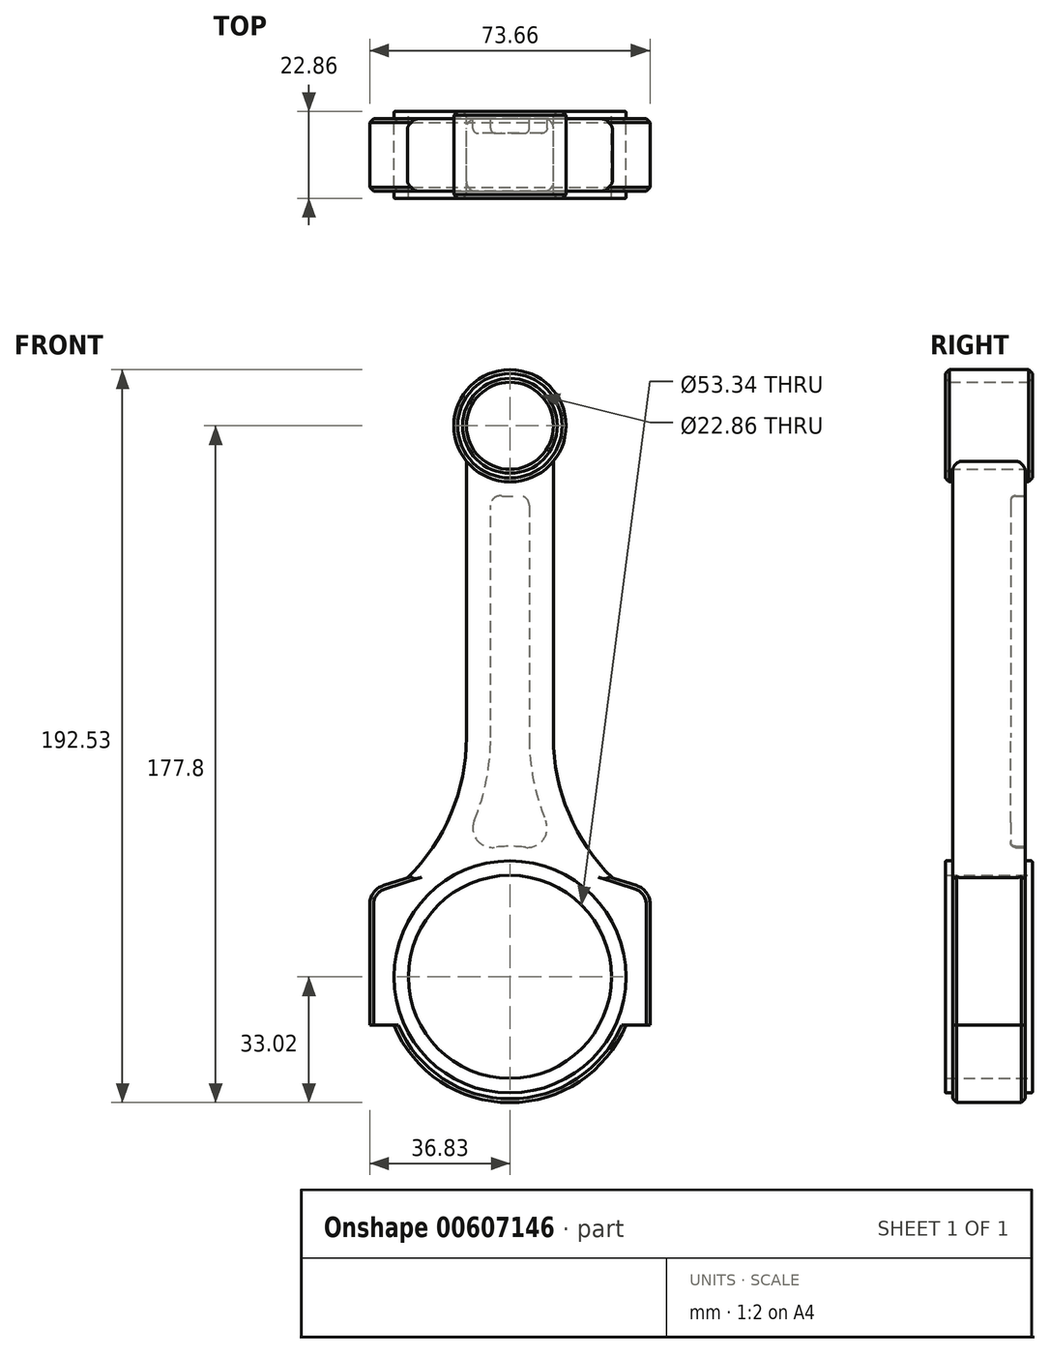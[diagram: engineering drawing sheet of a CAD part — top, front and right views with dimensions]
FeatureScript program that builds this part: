
annotation { "Feature Type Name" : "Feature", "Feature Type Description" : "" }
export const myFeature = defineFeature(function(context is Context, id is Id, definition is map)
    precondition{}
    {
        {
            var Q0;
            Q0=qCreatedBy(makeId("Front.planeOp"),FACE);
            var sketch = newSketch(context, id + "F0", { "sketchPlane" : qUnion([Q0])});
            skCircle(sketch, "E0", {"center": v(0, 0) * mm, "radius": 26.67 * mm});
            skCircle(sketch, "E1.0", {"center": v(0, 0) * mm, "radius": 30.48 * mm});
            skCircle(sketch, "E2.0", {"center": v(0, 0) * mm, "radius": 33.02 * mm});
            skLineSegment(sketch, "E3", {"start": v(-26.67, 0) * mm, "end": v(-36.83, 0) * mm});
            skLineSegment(sketch, "E4", {"start": v(-36.83, 0) * mm, "end": v(-36.83, 22.86) * mm});
            skLineSegment(sketch, "E5", {"start": v(0, 0) * mm, "end": v(0, 144.78) * mm, "construction": true});
            skCircle(sketch, "E6", {"center": v(0, 144.78) * mm, "radius": 11.43 * mm});
            skCircle(sketch, "E7.0", {"center": v(0, 144.78) * mm, "radius": 14.73 * mm});
            skLineSegment(sketch, "E8", {"start": v(-11.43, 144.78) * mm, "end": v(-11.43, 62.91) * mm});
            skLineSegment(sketch, "E9.MirrorCS", {"start": v(11.43, 144.78) * mm, "end": v(11.43, 62.91) * mm});
            skLineSegment(sketch, "E10.MirrorCS", {"start": v(36.83, 0) * mm, "end": v(36.83, 22.86) * mm});
            skLineSegment(sketch, "E11.MirrorCS", {"start": v(26.67, 0) * mm, "end": v(36.83, 0) * mm});
            skLineSegment(sketch, "E12", {"start": v(-36.83, 22.86) * mm, "end": v(-26.89, 26.05) * mm});
            skLineSegment(sketch, "E13.MirrorCS", {"start": v(36.83, 22.86) * mm, "end": v(26.89, 26.05) * mm});
            skArc(sketch, "E14", {"start": v(-26.89, 26.05) * mm, "mid": v(-15.45, 42.93) * mm, "end": v(-11.43, 62.91) * mm});
            skArc(sketch, "E15.MirrorCS", {"start": v(26.89, 26.05) * mm, "mid": v(15.45, 42.93) * mm, "end": v(11.43, 62.91) * mm});
            skLineSegment(sketch, "E16", {"start": v(-36.83, 0) * mm, "end": v(-36.83, -12.7) * mm});
            skLineSegment(sketch, "E17", {"start": v(-36.83, -12.7) * mm, "end": v(-30.48, -12.7) * mm});
            skLineSegment(sketch, "E18.MirrorCS", {"start": v(36.83, 0) * mm, "end": v(36.83, -12.7) * mm});
            skLineSegment(sketch, "E19.MirrorCS", {"start": v(36.83, -12.7) * mm, "end": v(30.48, -12.7) * mm});
            skSolve(sketch);
        }
        {
            var Q0;
            {var subQ13=sQuery(id+"F0.wireOp",EDGE,"E4");Q0=makeQuery(id+"F0.imprint","IMPRINT",FACE,{"disambiguationData":[TD([[makeQuery(id+"F0.imprint","IMPRINT",EDGE,{"derivedFrom":subQ13}),-1.0]])]});}
            var Q1;
            {var subQ0=sQuery(id+"F0.wireOp",EDGE,"E3");var subQ1=sQuery(id+"F0.wireOp",EDGE,"E1.0");var subQ2=makeQuery(id+"F0.imprint","INTERSECT",VERTEX,{"derivedFrom":[subQ1,subQ0]});Q1=makeQuery(id+"F0.imprint","IMPRINT",FACE,{"disambiguationData":[TD([[makeQuery(id+"F0.imprint","IMPRINT",EDGE,{"disambiguationData":[TD([[subQ2,1.0]])],"derivedFrom":subQ1}),-1.0]])]});}
            extrude(context, id + "F1", {"entities" : qUnion([Q0, Q1]), "depth" : 19.05 * mm, "offsetDistance" : 25.4 * mm, "symmetric" : true});
        }
        {
            var Q0;
            {var subQ4=sQuery(id+"F0.wireOp",EDGE,"E16");Q0=makeQuery(id+"F0.imprint","IMPRINT",FACE,{"disambiguationData":[TD([[makeQuery(id+"F0.imprint","IMPRINT",EDGE,{"derivedFrom":subQ4}),1.0]])]});}
            var Q1;
            {var subQ5=sQuery(id+"F0.wireOp",EDGE,"E3");var subQ7=sQuery(id+"F0.wireOp",EDGE,"E1.0");var subQ8=makeQuery(id+"F0.imprint","INTERSECT",VERTEX,{"derivedFrom":[subQ7,subQ5]});Q1=makeQuery(id+"F0.imprint","IMPRINT",FACE,{"disambiguationData":[TD([[makeQuery(id+"F0.imprint","IMPRINT",EDGE,{"disambiguationData":[TD([[subQ8,-1.0]])],"derivedFrom":subQ7}),-1.0]])]});}
            var Q2;
            {var subQ4=sQuery(id+"F0.wireOp",EDGE,"E18.MirrorCS");Q2=makeQuery(id+"F0.imprint","IMPRINT",FACE,{"disambiguationData":[TD([[makeQuery(id+"F0.imprint","IMPRINT",EDGE,{"derivedFrom":subQ4}),-1.0]])]});}
            extrude(context, id + "F2", {"entities" : qUnion([Q0, Q1, Q2]), "depth" : 19.05 * mm, "offsetDistance" : 25.4 * mm, "symmetric" : true});
        }
        {
            var Q0;
            {var subQ0=sQuery(id+"F0.wireOp",EDGE,"E3");var subQ1=sQuery(id+"F0.wireOp",EDGE,"E0");var subQ2=makeQuery(id+"F0.imprint","INTERSECT",VERTEX,{"derivedFrom":[subQ1,subQ0]});Q0=makeQuery(id+"F0.imprint","IMPRINT",FACE,{"disambiguationData":[TD([[makeQuery(id+"F0.imprint","IMPRINT",EDGE,{"disambiguationData":[TD([[subQ2,1.0]])],"derivedFrom":subQ1}),-1.0]])]});}
            extrude(context, id + "F3", {"entities" : qUnion([Q0]), "operationType" : NewBodyOperationType.ADD, "depth" : 22.86 * mm, "offsetDistance" : 25.4 * mm, "symmetric" : true});
        }
        {
            var Q0;
            {var subQ0=sQuery(id+"F0.wireOp",EDGE,"E3");var subQ1=sQuery(id+"F0.wireOp",EDGE,"E0");var subQ2=makeQuery(id+"F0.imprint","INTERSECT",VERTEX,{"derivedFrom":[subQ1,subQ0]});Q0=makeQuery(id+"F0.imprint","IMPRINT",FACE,{"disambiguationData":[TD([[makeQuery(id+"F0.imprint","IMPRINT",EDGE,{"disambiguationData":[TD([[subQ2,-1.0]])],"derivedFrom":subQ1}),-1.0]])]});}
            extrude(context, id + "F4", {"entities" : qUnion([Q0]), "operationType" : NewBodyOperationType.ADD, "depth" : 22.86 * mm, "offsetDistance" : 25.4 * mm, "symmetric" : true});
        }
        {
            var Q0;
            {var subQ0=sQuery(id+"F0.wireOp",EDGE,"E8");var subQ1=sQuery(id+"F0.wireOp",EDGE,"E6");var subQ2=makeQuery(id+"F0.imprint","INTERSECT",VERTEX,{"derivedFrom":[subQ1,subQ0]});Q0=makeQuery(id+"F0.imprint","IMPRINT",FACE,{"disambiguationData":[TD([[makeQuery(id+"F0.imprint","IMPRINT",EDGE,{"disambiguationData":[TD([[subQ2,1.0]])],"derivedFrom":subQ1}),-1.0]])]});}
            var Q1;
            {var subQ0=sQuery(id+"F0.wireOp",EDGE,"E8");var subQ1=sQuery(id+"F0.wireOp",EDGE,"E6");var subQ2=makeQuery(id+"F0.imprint","INTERSECT",VERTEX,{"derivedFrom":[subQ1,subQ0]});Q1=makeQuery(id+"F0.imprint","IMPRINT",FACE,{"disambiguationData":[TD([[makeQuery(id+"F0.imprint","IMPRINT",EDGE,{"disambiguationData":[TD([[subQ2,-1.0]])],"derivedFrom":subQ1}),-1.0]])]});}
            extrude(context, id + "F5", {"entities" : qUnion([Q0, Q1]), "operationType" : NewBodyOperationType.ADD, "depth" : 22.86 * mm, "offsetDistance" : 25.4 * mm, "symmetric" : true});
        }
        {
            var Q0;
            Q0=makeQuery(id+"F1.opExtrude","CAP_EDGE",EDGE,{"disambiguationData":[OSD([sQuery(id+"F0.wireOp",EDGE,"E9.MirrorCS")])],"isStart":true});
            var Q1;
            Q1=makeQuery(id+"F1.opExtrude","CAP_EDGE",EDGE,{"disambiguationData":[OSD([sQuery(id+"F0.wireOp",EDGE,"E8")])],"isStart":true});
            var Q2;
            Q2=makeQuery(id+"F1.opExtrude","CAP_EDGE",EDGE,{"disambiguationData":[OSD([sQuery(id+"F0.wireOp",EDGE,"E8")])],"isStart":false});
            var Q3;
            Q3=makeQuery(id+"F1.opExtrude","CAP_EDGE",EDGE,{"disambiguationData":[OSD([sQuery(id+"F0.wireOp",EDGE,"E9.MirrorCS")])],"isStart":false});
            fillet(context, id + "F6", {"entities" : qUnion([Q0, Q1, Q2, Q3]), "radius" : 2.54 * mm, "tangentPropagation" : true, "allowEdgeOverflow" : false});
        }
        {
            var Q0;
            Q0=makeQuery(id+"F1.opExtrude","CAP_FACE",FACE,{"disambiguationData":[OSD([sQuery(id+"F0.wireOp",EDGE,"E1.0"),sQuery(id+"F0.wireOp",EDGE,"E3"),sQuery(id+"F0.wireOp",EDGE,"E4"),sQuery(id+"F0.wireOp",EDGE,"E7.0"),sQuery(id+"F0.wireOp",EDGE,"E8"),sQuery(id+"F0.wireOp",EDGE,"E9.MirrorCS"),sQuery(id+"F0.wireOp",EDGE,"E10.MirrorCS"),sQuery(id+"F0.wireOp",EDGE,"E11.MirrorCS"),sQuery(id+"F0.wireOp",EDGE,"E12"),sQuery(id+"F0.wireOp",EDGE,"E13.MirrorCS"),sQuery(id+"F0.wireOp",EDGE,"E14"),sQuery(id+"F0.wireOp",EDGE,"E15.MirrorCS")])],"isStart":true});
            var sketch = newSketch(context, id + "F7", { "sketchPlane" : qUnion([Q0])});
            skLineSegment(sketch, "E20.0", {"start": v(-5.08, 123.85) * mm, "end": v(-5.08, 62.91) * mm});
            skArc(sketch, "E20.1", {"start": v(-4.07, 34.05) * mm, "mid": v(0, 34.3) * mm, "end": v(4.07, 34.05) * mm});
            skArc(sketch, "E20.2", {"start": v(9.37, 41) * mm, "mid": v(6.16, 51.75) * mm, "end": v(5.08, 62.91) * mm});
            skArc(sketch, "E20.3", {"start": v(-5.08, 62.91) * mm, "mid": v(-6.16, 51.75) * mm, "end": v(-9.37, 41) * mm});
            skLineSegment(sketch, "E20.4", {"start": v(5.08, 62.91) * mm, "end": v(5.08, 123.85) * mm});
            skArc(sketch, "E20.5", {"start": v(2.23, 126.37) * mm, "mid": v(0, 126.24) * mm, "end": v(-2.23, 126.37) * mm});
            skPoint(sketch, "E21.visualSharp", {"position": v(-14.64, 31) * mm});
            skArc(sketch, "E21.filletArc", {"start": v(-9.37, 41) * mm, "mid": v(-8.7, 36.01) * mm, "end": v(-4.07, 34.05) * mm});
            skPoint(sketch, "E22.visualSharp", {"position": v(14.64, 31) * mm});
            skArc(sketch, "E22.filletArc", {"start": v(4.07, 34.05) * mm, "mid": v(8.7, 36.01) * mm, "end": v(9.37, 41) * mm});
            skPoint(sketch, "E23.visualSharp", {"position": v(-5.08, 126.95) * mm});
            skArc(sketch, "E23.filletArc", {"start": v(-2.23, 126.37) * mm, "mid": v(-4.22, 125.75) * mm, "end": v(-5.08, 123.85) * mm});
            skPoint(sketch, "E24.visualSharp", {"position": v(5.08, 126.95) * mm});
            skArc(sketch, "E24.filletArc", {"start": v(5.08, 123.85) * mm, "mid": v(4.22, 125.75) * mm, "end": v(2.23, 126.37) * mm});
            skSolve(sketch);
        }
        {
            var Q0;
            Q0=makeQuery(id+"F7.imprint","IMPRINT",FACE,{"disambiguationData":[TD([[makeQuery(id+"F7.imprint","IMPRINT",EDGE,{"derivedFrom":sQuery(id+"F7.wireOp",EDGE,"E20.0")}),1.0]])]});
            extrude(context, id + "F8", {"entities" : qUnion([Q0]), "operationType" : NewBodyOperationType.REMOVE, "oppositeDirection" : true, "depth" : 3.8 * mm, "offsetDistance" : 25.4 * mm});
        }
        {
            var Q0;
            Q0=makeQuery(id+"F8.boolean.opBoolean","COPY",FACE,{"derivedFrom":makeQuery(id+"F8.opExtrude","CAP_FACE",FACE,{"disambiguationData":[OSD([sQuery(id+"F7.wireOp",EDGE,"E20.0"),sQuery(id+"F7.wireOp",EDGE,"E20.1"),sQuery(id+"F7.wireOp",EDGE,"E20.2"),sQuery(id+"F7.wireOp",EDGE,"E20.3"),sQuery(id+"F7.wireOp",EDGE,"E20.4"),sQuery(id+"F7.wireOp",EDGE,"E20.5"),sQuery(id+"F7.wireOp",EDGE,"E21.filletArc"),sQuery(id+"F7.wireOp",EDGE,"E22.filletArc"),sQuery(id+"F7.wireOp",EDGE,"E23.filletArc"),sQuery(id+"F7.wireOp",EDGE,"E24.filletArc")])],"isStart":false})});
            var Q1;
            Q1=makeQuery(id+"F8.boolean.opBoolean","COPY",EDGE,{"derivedFrom":makeQuery(id+"F8.opExtrude","CAP_EDGE",EDGE,{"disambiguationData":[OSD([sQuery(id+"F7.wireOp",EDGE,"E20.2")])],"isStart":true})});
            fillet(context, id + "F9", {"entities" : qUnion([Q0, Q1]), "radius" : 1.27 * mm, "tangentPropagation" : true, "allowEdgeOverflow" : false});
        }
        {
            var Q0;
            Q0=makeQuery(id+"F3.opExtrude","CAP_EDGE",EDGE,{"disambiguationData":[OSD([sQuery(id+"F0.wireOp",EDGE,"E0")])],"isStart":true});
            var Q1;
            Q1=makeQuery(id+"F3.opExtrude","CAP_EDGE",EDGE,{"disambiguationData":[OSD([sQuery(id+"F0.wireOp",EDGE,"E1.0")])],"isStart":true});
            var Q2;
            Q2=makeQuery(id+"F4.opExtrude","CAP_EDGE",EDGE,{"disambiguationData":[OSD([sQuery(id+"F0.wireOp",EDGE,"E0")])],"isStart":true});
            var Q3;
            Q3=makeQuery(id+"F4.opExtrude","CAP_EDGE",EDGE,{"disambiguationData":[OSD([sQuery(id+"F0.wireOp",EDGE,"E1.0")])],"isStart":true});
            var Q4;
            Q4=makeQuery(id+"F3.opExtrude","CAP_EDGE",EDGE,{"disambiguationData":[OSD([sQuery(id+"F0.wireOp",EDGE,"E1.0")])],"isStart":false});
            var Q5;
            Q5=makeQuery(id+"F3.opExtrude","CAP_EDGE",EDGE,{"disambiguationData":[OSD([sQuery(id+"F0.wireOp",EDGE,"E0")])],"isStart":false});
            var Q6;
            Q6=makeQuery(id+"F4.opExtrude","CAP_EDGE",EDGE,{"disambiguationData":[OSD([sQuery(id+"F0.wireOp",EDGE,"E0")])],"isStart":false});
            var Q7;
            Q7=makeQuery(id+"F4.opExtrude","CAP_EDGE",EDGE,{"disambiguationData":[OSD([sQuery(id+"F0.wireOp",EDGE,"E1.0")])],"isStart":false});
            fillet(context, id + "F10", {"entities" : qUnion([Q0, Q1, Q2, Q3, Q4, Q5, Q6, Q7]), "radius" : 0.25 * mm, "tangentPropagation" : true, "allowEdgeOverflow" : false});
        }
        {
            var Q0;
            Q0=makeQuery(id+"F1.opExtrude","SWEPT_EDGE",EDGE,{"disambiguationData":[OSD([sQuery(id+"F0.wireOp",EDGE,"E10.MirrorCS"),sQuery(id+"F0.wireOp",EDGE,"E13.MirrorCS")])]});
            var Q1;
            Q1=makeQuery(id+"F1.opExtrude","SWEPT_EDGE",EDGE,{"disambiguationData":[OSD([sQuery(id+"F0.wireOp",EDGE,"E4"),sQuery(id+"F0.wireOp",EDGE,"E12")])]});
            fillet(context, id + "F11", {"entities" : qUnion([Q0, Q1]), "radius" : 5.08 * mm, "tangentPropagation" : true, "allowEdgeOverflow" : false});
        }
        {
            var Q0;
            Q0=makeQuery(id+"F2.opExtrude","CAP_EDGE",EDGE,{"disambiguationData":[OSD([sQuery(id+"F0.wireOp",EDGE,"E16")])],"isStart":false});
            var Q1;
            Q1=makeQuery(id+"F1.opExtrude","CAP_EDGE",EDGE,{"disambiguationData":[OSD([sQuery(id+"F0.wireOp",EDGE,"E4")])],"isStart":false});
            var Q2;
            Q2=makeQuery(id+"F2.opExtrude","CAP_EDGE",EDGE,{"disambiguationData":[OSD([sQuery(id+"F0.wireOp",EDGE,"E16")])],"isStart":true});
            var Q3;
            Q3=makeQuery(id+"F1.opExtrude","CAP_EDGE",EDGE,{"disambiguationData":[OSD([sQuery(id+"F0.wireOp",EDGE,"E4")])],"isStart":true});
            var Q4;
            Q4=makeQuery(id+"F1.opExtrude","CAP_EDGE",EDGE,{"disambiguationData":[OSD([sQuery(id+"F0.wireOp",EDGE,"E10.MirrorCS")])],"isStart":true});
            var Q5;
            Q5=makeQuery(id+"F2.opExtrude","CAP_EDGE",EDGE,{"disambiguationData":[OSD([sQuery(id+"F0.wireOp",EDGE,"E18.MirrorCS")])],"isStart":true});
            var Q6;
            Q6=makeQuery(id+"F1.opExtrude","CAP_EDGE",EDGE,{"disambiguationData":[OSD([sQuery(id+"F0.wireOp",EDGE,"E10.MirrorCS")])],"isStart":false});
            var Q7;
            Q7=makeQuery(id+"F2.opExtrude","CAP_EDGE",EDGE,{"disambiguationData":[OSD([sQuery(id+"F0.wireOp",EDGE,"E18.MirrorCS")])],"isStart":false});
            var Q8;
            Q8=makeQuery(id+"F2.opExtrude","CAP_EDGE",EDGE,{"disambiguationData":[OSD([sQuery(id+"F0.wireOp",EDGE,"E2.0")])],"isStart":false});
            var Q9;
            Q9=makeQuery(id+"F2.opExtrude","CAP_EDGE",EDGE,{"disambiguationData":[OSD([sQuery(id+"F0.wireOp",EDGE,"E2.0")])],"isStart":true});
            var Q10;
            Q10=makeQuery(id+"F1.opExtrude","CAP_EDGE",EDGE,{"disambiguationData":[OSD([sQuery(id+"F0.wireOp",EDGE,"E1.0")])],"isStart":false});
            var Q11;
            Q11=makeQuery(id+"F2.opExtrude","CAP_EDGE",EDGE,{"disambiguationData":[OSD([sQuery(id+"F0.wireOp",EDGE,"E1.0")])],"isStart":false});
            var Q12;
            Q12=makeQuery(id+"F5.opExtrude","CAP_FACE",FACE,{"disambiguationData":[OSD([sQuery(id+"F0.wireOp",EDGE,"E6"),sQuery(id+"F0.wireOp",EDGE,"E7.0")])],"isStart":false});
            var Q13;
            Q13=makeQuery(id+"F5.opExtrude","CAP_EDGE",EDGE,{"disambiguationData":[OSD([sQuery(id+"F0.wireOp",EDGE,"E6")])],"isStart":true});
            var Q14;
            Q14=makeQuery(id+"F5.opExtrude","CAP_EDGE",EDGE,{"disambiguationData":[OSD([sQuery(id+"F0.wireOp",EDGE,"E7.0")])],"isStart":true});
            chamfer(context, id + "F12", {"entities" : qUnion([Q0, Q1, Q2, Q3, Q4, Q5, Q6, Q7, Q8, Q9, Q10, Q11, Q12, Q13, Q14]), "width" : 1.02 * mm, "tangentPropagation" : true});
        }
    });
